FCSTD DOCUMENT  (FreeCAD 0.17R12920 (Git))
Label: quadratic-bspline-study
License: All rights reserved
LicenseURL: http://en.wikipedia.org/wiki/All_rights_reserved
objects: Sketcher::SketchObject×1, PartDesign::Body×1
note: 2 computed .brp shape members not serialized (recipe doc carries the construction recipe); baked Part::Feature solids carry a one-line shape summary decoded from their .brp

FEATURE [Sketcher::SketchObject] Sketch
  MapMode = 5
  Support = -> [XY_Plane]
  sketch-geometry (24):
    g0-g3: Circle [constr] x4 (B-spline internal-alignment scaffolding for g4; pole/knot coordinates omitted)
    g4: BSplineCurve PolesCount=4 KnotsCount=2 Degree=3 IsPeriodic=0
    g5: GeomPoint [constr] X=-100 Y=0.0314931 Z=0
    g6: GeomPoint [constr] X=0 Y=100 Z=0
    g7: LineSegment [constr] StartX=-55.2285 StartY=99.9748 StartZ=0 EndX=0 EndY=100 EndZ=0
    g8: LineSegment [constr] StartX=-100 StartY=55.26 StartZ=0 EndX=-100 EndY=0.0314931 EndZ=0
    g9-g12: Circle [constr] x4 (B-spline internal-alignment scaffolding for g13; pole/knot coordinates omitted)
    g13: BSplineCurve PolesCount=4 KnotsCount=2 Degree=3 IsPeriodic=0
    g14: GeomPoint [constr] X=100 Y=0.0470183 Z=0
    g15: GeomPoint [constr] X=0 Y=100 Z=0
    g16: LineSegment [constr] StartX=55.2285 StartY=100.025 StartZ=0 EndX=0 EndY=100 EndZ=0
    g17: LineSegment [constr] StartX=100 StartY=55.2755 StartZ=0 EndX=100 EndY=0.0470183 EndZ=0
    g18: Circle [constr] CenterX=0 CenterY=0 CenterZ=0 NormalX=0 NormalY=0 NormalZ=1 AngleXU=0 Radius=94.8683
    g19: ArcOfEllipse CenterX=-192.589 CenterY=90 CenterZ=0 NormalX=0 NormalY=0 NormalZ=1 MajorRadius=41.8404 MinorRadius=17.385 AngleXU=0.362667 StartAngle=4.16994 EndAngle=7.26248
    g20: LineSegment [constr] StartX=-153.47 StartY=104.844 StartZ=0 EndX=-231.708 EndY=75.1563 EndZ=0
    g21: LineSegment [constr] StartX=-198.757 StartY=106.254 StartZ=0 EndX=-186.421 EndY=73.7458 EndZ=0
    g22: GeomPoint X=-157.007 Y=103.502 Z=0
    g23: GeomPoint X=-228.171 Y=76.4983 Z=0
  constraints (30):
    c: Equal(g0,g1)
    c: Equal(g0,g2)
    c: Equal(g0,g3)
    c: InternalAlignment(g0-g3 -> g4) x4
    c: InternalAlignment(g5,g4)
    c: InternalAlignment(g6,g4)
    c: Radius(g0) = 3
    c: Coincident(g7,g2)
    c: Coincident(g7,g3)
    c: Coincident(g8,g1)
    c: Coincident(g8,g0)
    c: Distance(g7) = 55.2285
    c: Equal(g7,g8)
    c: Equal(g9,g10)
    c: Equal(g9,g11)
    c: Equal(g9,g12)
    c: InternalAlignment(g9-g12 -> g13) x4
    c: InternalAlignment(g14,g13)
    c: InternalAlignment(g15,g13)
    c: Equal(g0,g9) = 3
    c: Coincident(g16,g11)
    c: Coincident(g16,g12)
    c: Coincident(g17,g10)
    c: Coincident(g17,g9)
    c: Equal(g7,g16) = 55.2285
    c: Equal(g16,g17)
    c: Coincident(g12,g3)
    c: Tangent(g7,g16)
    c: Coincident(g18,g-1)
    c: InternalAlignment(g20-g23 -> g19) x4
FEATURE [PartDesign::Body] Body
  Group = -> [Sketch]
  Origin = -> Origin
